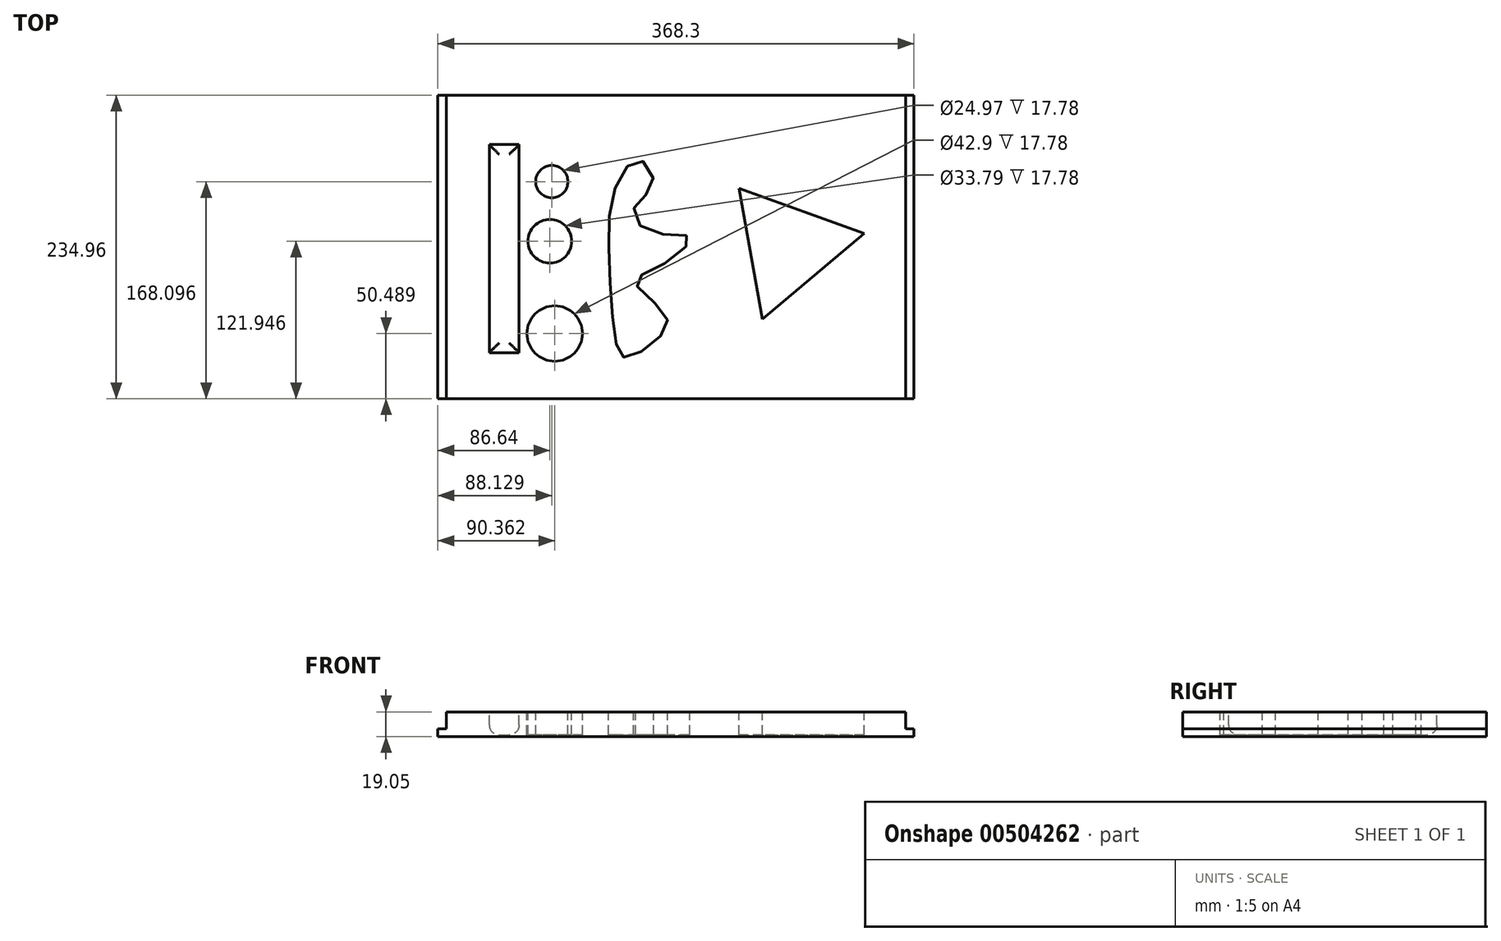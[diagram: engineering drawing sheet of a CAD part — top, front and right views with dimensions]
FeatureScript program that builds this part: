
annotation { "Feature Type Name" : "Feature", "Feature Type Description" : "" }
export const myFeature = defineFeature(function(context is Context, id is Id, definition is map)
    precondition{}
    {
        {
            var Q0;
            Q0=qCreatedBy(makeId("Top.planeOp"),FACE);
            var sketch = newSketch(context, id + "F0", { "sketchPlane" : qUnion([Q0])});
            skLineSegment(sketch, "E0.bottom", {"start": v(184.15, -117.47) * mm, "end": v(-184.15, -117.48) * mm});
            skLineSegment(sketch, "E0.top", {"start": v(184.15, 117.48) * mm, "end": v(-184.15, 117.47) * mm});
            skLineSegment(sketch, "E0.left", {"start": v(184.15, -117.47) * mm, "end": v(184.15, 117.48) * mm});
            skLineSegment(sketch, "E0.right", {"start": v(-184.15, -117.48) * mm, "end": v(-184.15, 117.47) * mm});
            skPoint(sketch, "E0.middle", {"position": v(0, 0) * mm});
            skSolve(sketch);
        }
        {
            var Q0;
            Q0=makeQuery(id+"F0.imprint","IMPRINT",FACE,{"disambiguationData":[TD([[makeQuery(id+"F0.imprint","IMPRINT",EDGE,{"derivedFrom":sQuery(id+"F0.wireOp",EDGE,"E0.bottom")}),-1.0]])]});
            extrude(context, id + "F1", {"entities" : qUnion([Q0]), "depth" : 19.05 * mm});
        }
        {
            var Q0;
            Q0=makeQuery(id+"F1.opExtrude","SWEPT_FACE",FACE,{"disambiguationData":[OSD([sQuery(id+"F0.wireOp",EDGE,"E0.bottom")])]});
            var sketch = newSketch(context, id + "F2", { "sketchPlane" : qUnion([Q0])});
            skLineSegment(sketch, "E1.bottom", {"start": v(184.15, 19.05) * mm, "end": v(177.55, 19.05) * mm});
            skLineSegment(sketch, "E1.top", {"start": v(184.15, 6.1) * mm, "end": v(177.55, 6.1) * mm});
            skLineSegment(sketch, "E1.left", {"start": v(184.15, 19.05) * mm, "end": v(184.15, 6.1) * mm});
            skLineSegment(sketch, "E1.right", {"start": v(177.55, 19.05) * mm, "end": v(177.55, 6.1) * mm});
            skLineSegment(sketch, "E2.bottom", {"start": v(-184.15, 19.05) * mm, "end": v(-177.55, 19.05) * mm});
            skLineSegment(sketch, "E2.top", {"start": v(-184.15, 6.1) * mm, "end": v(-177.55, 6.1) * mm});
            skLineSegment(sketch, "E2.left", {"start": v(-184.15, 19.05) * mm, "end": v(-184.15, 6.1) * mm});
            skLineSegment(sketch, "E2.right", {"start": v(-177.55, 19.05) * mm, "end": v(-177.55, 6.1) * mm});
            skSolve(sketch);
        }
        {
            var Q0;
            Q0=makeQuery(id+"F2.imprint","IMPRINT",FACE,{"disambiguationData":[TD([[makeQuery(id+"F2.imprint","IMPRINT",EDGE,{"derivedFrom":sQuery(id+"F2.wireOp",EDGE,"E1.bottom")}),1.0]])]});
            var Q1;
            Q1=makeQuery(id+"F2.imprint","IMPRINT",FACE,{"disambiguationData":[TD([[makeQuery(id+"F2.imprint","IMPRINT",EDGE,{"derivedFrom":sQuery(id+"F2.wireOp",EDGE,"E2.bottom")}),1.0]])]});
            extrude(context, id + "F3", {"entities" : qUnion([Q0, Q1]), "operationType" : NewBodyOperationType.REMOVE, "endBound" : BoundingType.THROUGH_ALL, "oppositeDirection" : true, "depth" : 25.4 * mm});
        }
        {
            var Q0;
            Q0=makeQuery(id+"F1.opExtrude","CAP_FACE",FACE,{"disambiguationData":[OSD([sQuery(id+"F0.wireOp",EDGE,"E0.bottom"),sQuery(id+"F0.wireOp",EDGE,"E0.top"),sQuery(id+"F0.wireOp",EDGE,"E0.left"),sQuery(id+"F0.wireOp",EDGE,"E0.right")])],"isStart":false});
            var sketch = newSketch(context, id + "F4", { "sketchPlane" : qUnion([Q0])});
            skLineSegment(sketch, "E3.bottom", {"start": v(-144.4, -81.88) * mm, "end": v(-121.33, -81.88) * mm});
            skLineSegment(sketch, "E3.top", {"start": v(-144.4, 79.27) * mm, "end": v(-121.33, 79.27) * mm});
            skLineSegment(sketch, "E3.left", {"start": v(-144.4, -81.88) * mm, "end": v(-144.4, 79.27) * mm});
            skLineSegment(sketch, "E3.right", {"start": v(-121.33, -81.88) * mm, "end": v(-121.33, 79.27) * mm});
            skCircle(sketch, "E4", {"center": v(-93.79, -67) * mm, "radius": 21.45 * mm});
            skCircle(sketch, "E5", {"center": v(-105.33, -35.36) * mm, "radius": 7.34 * mm});
            skCircle(sketch, "E6", {"center": v(-90.44, -27.91) * mm, "radius": 6.6 * mm});
            skCircle(sketch, "E7", {"center": v(-97.5, 4.47) * mm, "radius": 16.9 * mm});
            skCircle(sketch, "E8", {"center": v(-96.02, 50.62) * mm, "radius": 12.48 * mm});
            skCircle(sketch, "E9", {"center": v(-105.33, 74.06) * mm, "radius": 8.5 * mm});
            skFitSpline(sketch, "E10", {"points": [v(-46.15, -75.18) * mm, v(-51.73, -9.68) * mm, v(-45.78, 48.75) * mm, v(-27.17, 67) * mm, v(-17.86, 47.64) * mm, v(-32, 31.26) * mm, v(-21.21, 12.28) * mm, v(10.42, 7.44) * mm, v(-10.05, -13.4) * mm, v(-31.26, -27.54) * mm, v(-8.56, -51.73) * mm, v(-11.17, -68.1) * mm, v(-38.7, -85.6) * mm, v(-46.15, -75.18) * mm]});
            skCircle(sketch, "E11.cCircle", {"center": v(87.09, 0) * mm, "radius": 29.67 * mm, "construction": true});
            skLineSegment(sketch, "E11.0", {"start": v(48.8, 45.32) * mm, "end": v(145.48, 10.5) * mm});
            skLineSegment(sketch, "E11.1", {"start": v(145.48, 10.5) * mm, "end": v(67, -55.83) * mm});
            skLineSegment(sketch, "E11.2", {"start": v(67, -55.83) * mm, "end": v(48.8, 45.32) * mm});
            skPoint(sketch, "E11.0.midPoint", {"position": v(97.14, 27.91) * mm});
            skSolve(sketch);
        }
        {
            var Q0;
            Q0=makeQuery(id+"F4.imprint","IMPRINT",FACE,{"disambiguationData":[TD([[makeQuery(id+"F4.imprint","IMPRINT",EDGE,{"derivedFrom":sQuery(id+"F4.wireOp",EDGE,"E10")}),-1.0]])]});
            var Q1;
            Q1=makeQuery(id+"F4.imprint","IMPRINT",FACE,{"disambiguationData":[TD([[makeQuery(id+"F4.imprint","IMPRINT",EDGE,{"derivedFrom":sQuery(id+"F4.wireOp",EDGE,"E7")}),1.0]])]});
            var Q2;
            Q2=makeQuery(id+"F4.imprint","IMPRINT",FACE,{"disambiguationData":[TD([[makeQuery(id+"F4.imprint","IMPRINT",EDGE,{"derivedFrom":sQuery(id+"F4.wireOp",EDGE,"E4")}),1.0]])]});
            var Q3;
            Q3=makeQuery(id+"F4.imprint","IMPRINT",FACE,{"disambiguationData":[TD([[makeQuery(id+"F4.imprint","IMPRINT",EDGE,{"derivedFrom":sQuery(id+"F4.wireOp",EDGE,"E3.bottom")}),1.0]])]});
            var Q4;
            Q4=makeQuery(id+"F4.imprint","IMPRINT",FACE,{"disambiguationData":[TD([[makeQuery(id+"F4.imprint","IMPRINT",EDGE,{"derivedFrom":sQuery(id+"F4.wireOp",EDGE,"E8")}),1.0]])]});
            var Q5;
            Q5=makeQuery(id+"F4.imprint","IMPRINT",FACE,{"disambiguationData":[TD([[makeQuery(id+"F4.imprint","IMPRINT",EDGE,{"derivedFrom":sQuery(id+"F4.wireOp",EDGE,"E11.0")}),-1.0]])]});
            extrude(context, id + "F5", {"entities" : qUnion([Q0, Q1, Q2, Q3, Q4, Q5]), "operationType" : NewBodyOperationType.REMOVE, "oppositeDirection" : true, "depth" : 17.78 * mm});
        }
        {
            var Q0;
            Q0=makeQuery(id+"F5.boolean.opBoolean","COPY",FACE,{"derivedFrom":makeQuery(id+"F5.opExtrude","CAP_FACE",FACE,{"disambiguationData":[OSD([sQuery(id+"F4.wireOp",EDGE,"E3.bottom"),sQuery(id+"F4.wireOp",EDGE,"E3.top"),sQuery(id+"F4.wireOp",EDGE,"E3.left"),sQuery(id+"F4.wireOp",EDGE,"E3.right")])],"isStart":false})});
            fillet(context, id + "F6", {"entities" : qUnion([Q0]), "radius" : 7.62 * mm, "tangentPropagation" : true, "allowEdgeOverflow" : false});
        }
        {
            var Q0;
            Q0=qCreatedBy(makeId("Right.planeOp"),FACE);
            var sketch = newSketch(context, id + "F7", { "sketchPlane" : qUnion([Q0])});
            skLineSegment(sketch, "E12", {"start": v(8.59, 71.95) * mm, "end": v(-19.05, 71.95) * mm});
            skLineSegment(sketch, "E13", {"start": v(-19.05, 71.95) * mm, "end": v(0, 91) * mm});
            skLineSegment(sketch, "E14", {"start": v(0, 91) * mm, "end": v(8.59, 91) * mm});
            skLineSegment(sketch, "E15", {"start": v(8.59, 91) * mm, "end": v(8.59, 71.95) * mm});
            skLineSegment(sketch, "E16", {"start": v(-12.7, 71.95) * mm, "end": v(0, 84.65) * mm});
            skLineSegment(sketch, "E17", {"start": v(0, 84.65) * mm, "end": v(8.59, 84.65) * mm});
            skSolve(sketch);
        }
        {
            var Q0;
            Q0=makeQuery(id+"F7.imprint","IMPRINT",FACE,{"disambiguationData":[TD([[makeQuery(id+"F7.imprint","IMPRINT",EDGE,{"derivedFrom":sQuery(id+"F7.wireOp",EDGE,"E12")}),-1.0]])]});
            var Q1;
            {var subQ3=sQuery(id+"F7.wireOp",EDGE,"E13");Q1=makeQuery(id+"F7.imprint","IMPRINT",FACE,{"disambiguationData":[TD([[makeQuery(id+"F7.imprint","IMPRINT",EDGE,{"derivedFrom":subQ3}),-1.0]])]});}
            extrude(context, id + "F8", {"entities" : qUnion([Q0, Q1]), "depth" : 101.6 * mm, "offsetDistance" : 25.4 * mm});
        }
        {
            var Q0;
            Q0=makeQuery(id+"F8.opExtrude","SWEPT_EDGE",EDGE,{"disambiguationData":[OSD([sQuery(id+"F7.wireOp",EDGE,"E12"),sQuery(id+"F7.wireOp",EDGE,"E13")])]});
            cPoint(context, id + "F9", {"entities" : qUnion([Q0]), "parameter" : 0.5});
        }
        {
            var Q0;
            Q0=makeQuery(id+"F8.opExtrude","SWEPT_EDGE",EDGE,{"disambiguationData":[OSD([sQuery(id+"F7.wireOp",EDGE,"E13"),sQuery(id+"F7.wireOp",EDGE,"E14")])]});
            cPoint(context, id + "F10", {"entities" : qUnion([Q0]), "parameter" : 0.5});
        }
        {
            var Q0;
            Q0=makeQuery(id+"F8.opExtrude","SWEPT_EDGE",EDGE,{"disambiguationData":[OSD([sQuery(id+"F7.wireOp",EDGE,"E12"),sQuery(id+"F7.wireOp",EDGE,"E15")])]});
            cPoint(context, id + "F11", {"entities" : qUnion([Q0]), "parameter" : 0.5});
        }
        {
            var Q0;
            Q0 = qCreatedBy(id + "F9" ,VERTEX);
            var Q1;
            Q1 = qCreatedBy(id + "F10" ,VERTEX);
            var Q2;
            Q2 = qCreatedBy(id + "F11" ,VERTEX);
            cPlane(context, id + "F12", {"entities" : qUnion([Q0, Q1, Q2]), "cplaneType" : CPlaneType.THREE_POINT, "offset" : 25.4 * mm, "width" : 152.4 * mm, "height" : 152.4 * mm});
        }
        {
            var Q0;
            Q0=qCreatedBy(id+"F12.planeOp",FACE);
            var sketch = newSketch(context, id + "F13", { "sketchPlane" : qUnion([Q0])});
            skLineSegment(sketch, "E18", {"start": v(-17.3, 70.08) * mm, "end": v(0, 86.98) * mm});
            skLineSegment(sketch, "E19", {"start": v(0, 86.98) * mm, "end": v(10.1, 86.98) * mm});
            skLineSegment(sketch, "E20", {"start": v(10.1, 86.98) * mm, "end": v(10.74, 68.8) * mm});
            skLineSegment(sketch, "E21", {"start": v(10.74, 68.8) * mm, "end": v(-17.3, 70.08) * mm});
            skSolve(sketch);
        }
        {
            var Q0;
            Q0=makeQuery(id+"F13.imprint","IMPRINT",FACE,{"disambiguationData":[TD([[makeQuery(id+"F13.imprint","IMPRINT",EDGE,{"derivedFrom":sQuery(id+"F13.wireOp",EDGE,"E18")}),-1.0]])]});
            extrude(context, id + "F14", {"entities" : qUnion([Q0]), "operationType" : NewBodyOperationType.REMOVE, "endBound" : BoundingType.SYMMETRIC, "oppositeDirection" : true, "depth" : 88.9 * mm, "offsetDistance" : 25.4 * mm});
        }
        {
            var Q0;
            Q0=makeQuery(id+"F8.opExtrude","SWEPT_BODY",BODY,{"disambiguationData":[OSD([sQuery(id+"F7.wireOp",EDGE,"E12"),sQuery(id+"F7.wireOp",EDGE,"E13"),sQuery(id+"F7.wireOp",EDGE,"E14"),sQuery(id+"F7.wireOp",EDGE,"E15")])]});
            transform(context, id + "F15", {"entities" : qUnion([Q0]), "transformType" : TransformType.TRANSLATION_3D, "dx" : 0 * mm, "dy" : 0 * mm, "dz" : 0 * mm, "makeCopy" : true});
        }
        {
            var Q0;
            Q0=makeQuery(id+"F8.opExtrude","SWEPT_BODY",BODY,{"disambiguationData":[OSD([sQuery(id+"F7.wireOp",EDGE,"E12"),sQuery(id+"F7.wireOp",EDGE,"E13"),sQuery(id+"F7.wireOp",EDGE,"E14"),sQuery(id+"F7.wireOp",EDGE,"E15")])]});
            deleteBodies(context, id + "F16", {"entities" : qUnion([Q0])});
        }
        {
            var Q0;
            Q0=makeQuery(id+"F15.opPattern","COPY",BODY,{"derivedFrom":makeQuery(id+"F8.opExtrude","SWEPT_BODY",BODY,{"disambiguationData":[OSD([sQuery(id+"F7.wireOp",EDGE,"E12"),sQuery(id+"F7.wireOp",EDGE,"E13"),sQuery(id+"F7.wireOp",EDGE,"E14"),sQuery(id+"F7.wireOp",EDGE,"E15")])]}),"instanceName":"1"});
            deleteBodies(context, id + "F17", {"entities" : qUnion([Q0])});
        }
    });
